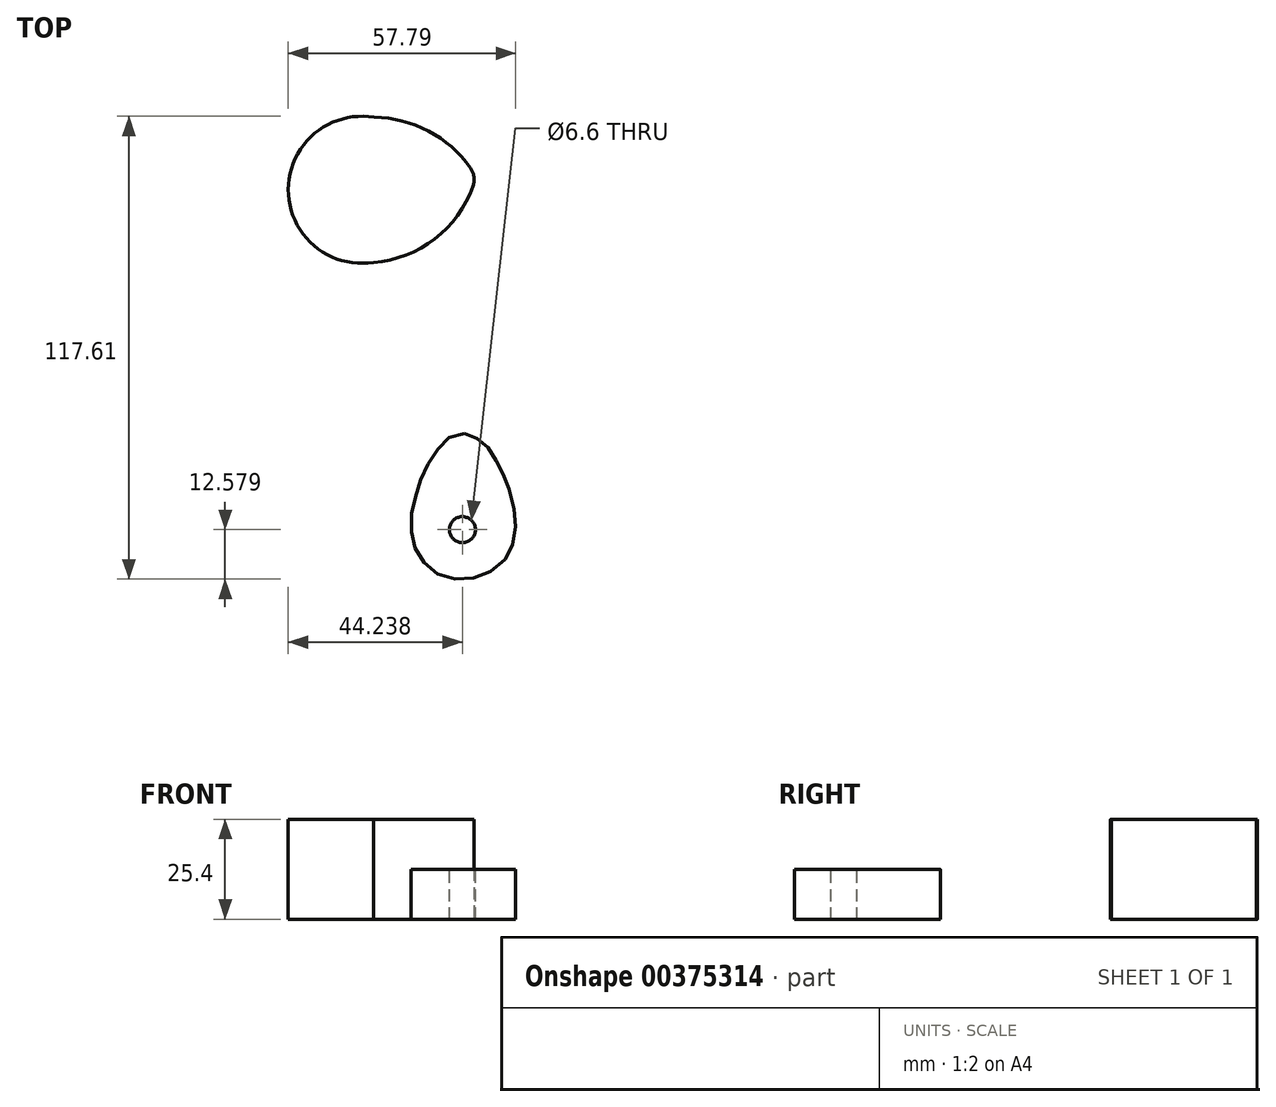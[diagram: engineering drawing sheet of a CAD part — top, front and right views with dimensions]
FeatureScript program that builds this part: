
annotation { "Feature Type Name" : "Feature", "Feature Type Description" : "" }
export const myFeature = defineFeature(function(context is Context, id is Id, definition is map)
    precondition{}
    {
        {
            var Q0;
            Q0=qCreatedBy(makeId("Top.planeOp"),FACE);
            var sketch = newSketch(context, id + "F0", { "sketchPlane" : qUnion([Q0])});
            skFitSpline(sketch, "E0", {"points": [v(-12.9, -21.8) * mm, v(-11.05, -22.23) * mm, v(-9.02, -23.56) * mm, v(-7.26, -25.06) * mm, v(-5.75, -27.44) * mm, v(-4.43, -29.47) * mm, v(-3.28, -31.77) * mm, v(-2.22, -34.15) * mm, v(-0.9, -38.3) * mm, v(0, -42.8) * mm, v(0, -46.06) * mm, v(-0.81, -50.21) * mm, v(-2.05, -52.86) * mm, v(-4.43, -55.6) * mm, v(-8.05, -57.72) * mm, v(-11.76, -58.69) * mm, v(-15.73, -58.69) * mm, v(-19.26, -57.72) * mm, v(-22.26, -55.6) * mm, v(-24.47, -52.95) * mm, v(-25.88, -49.86) * mm, v(-26.4, -46.86) * mm, v(-26.4, -42.8) * mm, v(-25.88, -39.8) * mm, v(-24.82, -36) * mm, v(-23.94, -33.09) * mm, v(-22.26, -29.74) * mm, v(-20.14, -26.38) * mm, v(-18.38, -24) * mm, v(-15.82, -22.23) * mm, v(-12.9, -21.8) * mm]});
            skSolve(sketch);
        }
        {
            var Q0;
            Q0 = qSketchRegion(id + "F0", true);
            extrude(context, id + "F1", {"entities" : qUnion([Q0]), "depth" : 12.7 * mm});
        }
        {
            var Q0;
            Q0=makeQuery(id+"F1.opExtrude","CAP_FACE",FACE,{"disambiguationData":[OSD([sQuery(id+"F0.wireOp",EDGE,"E0")])],"isStart":false});
            var sketch = newSketch(context, id + "F2", { "sketchPlane" : qUnion([Q0])});
            skCircle(sketch, "E1", {"center": v(-13.46, -46.23) * mm, "radius": 3.3 * mm});
            skSolve(sketch);
        }
        {
            var Q0;
            Q0 = qSketchRegion(id + "F2", true);
            extrude(context, id + "F3", {"entities" : qUnion([Q0]), "operationType" : NewBodyOperationType.REMOVE, "oppositeDirection" : true, "depth" : 12.7 * mm});
        }
        {
            var Q0;
            Q0=qCreatedBy(makeId("Top.planeOp"),FACE);
            var sketch = newSketch(context, id + "F4", { "sketchPlane" : qUnion([Q0])});
            skArc(sketch, "E2", {"start": v(-35.87, 58.53) * mm, "mid": v(-57.7, 40.22) * mm, "end": v(-36.06, 21.68) * mm});
            skArc(sketch, "E3", {"start": v(-10.05, 43.55) * mm, "mid": v(-21, 54.43) * mm, "end": v(-35.87, 58.53) * mm});
            skArc(sketch, "E4", {"start": v(-36.06, 21.68) * mm, "mid": v(-19.52, 28.41) * mm, "end": v(-10.05, 43.55) * mm});
            skSolve(sketch);
        }
        {
            var Q0;
            Q0 = qSketchRegion(id + "F4", true);
            extrude(context, id + "F5", {"entities" : qUnion([Q0]), "depth" : 25.4 * mm});
        }
        {
            var Q0;
            Q0=makeQuery(id+"F5.opExtrude","SWEPT_EDGE",EDGE,{"disambiguationData":[OSD([sQuery(id+"F4.wireOp",EDGE,"E3"),sQuery(id+"F4.wireOp",EDGE,"E4")])]});
            fillet(context, id + "F6", {"entities" : qUnion([Q0]), "radius" : 5.08 * mm, "tangentPropagation" : true, "allowEdgeOverflow" : false});
        }
    });
